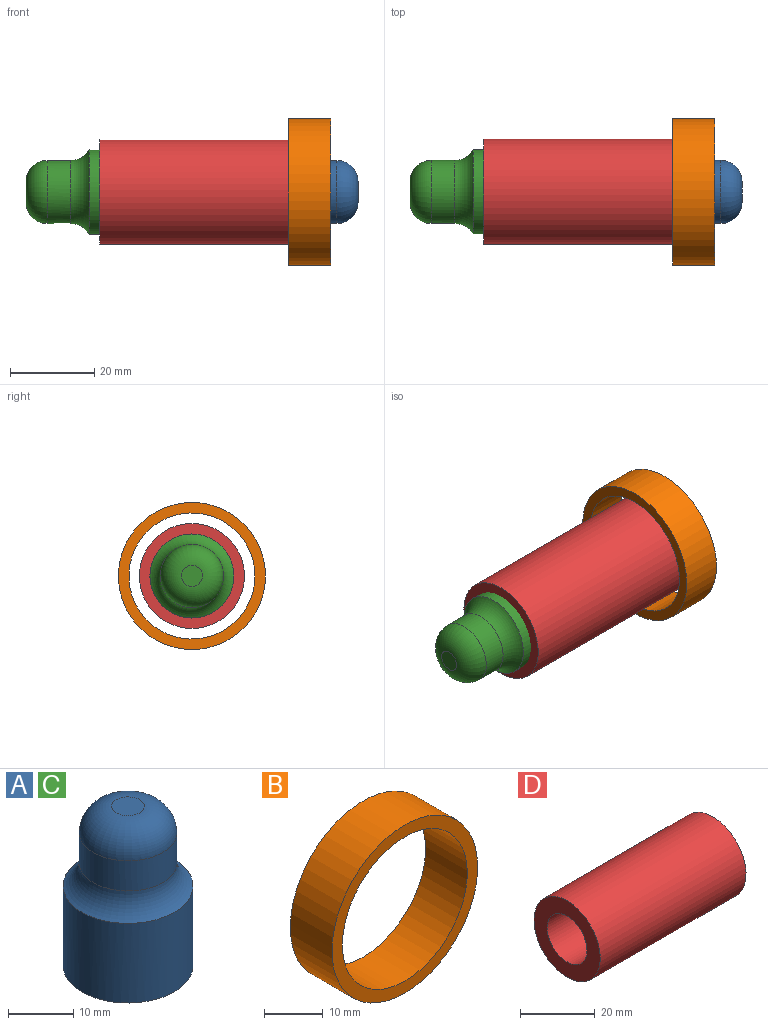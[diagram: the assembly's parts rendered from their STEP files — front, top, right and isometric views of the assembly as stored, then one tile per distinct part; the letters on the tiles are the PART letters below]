
ASSEMBLY  parts=4 mates=3
PART A: 6 faces, bbox 27.1x27.1x30 mm
  f0: cylinder r=10mm len=20mm, axis (0,0,-1), area 942.5mm2, adj f1,f4
  f1: plane 20x20mm, normal (0,0,-1), area 314.2mm2, adj f0
  f2: cylinder r=7.5mm len=15mm, axis (0,0,-1), area 267.2mm2, adj f4,f5
  f3: plane 5x5mm, normal (0,0,1), area 19.6mm2, adj f5
  f4: torus R=12.5mm, axis (0,0,-1), area 275.2mm2, adj f0,f2
  f5: torus R=2.5mm, axis (0,0,1), area 280.4mm2, adj f2,f3
PART B: 4 faces, bbox 35x10x35 mm
  f0: cylinder r=15mm len=30mm, axis (0,-1,0), area 942.5mm2, adj f2,f3
  f1: cylinder r=17.5mm len=35mm, axis (0,-1,0), area 1099.6mm2, adj f2,f3
  f2: plane 35x35mm, normal (0,1,0), area 255.3mm2, adj f0,f1
  f3: plane 35x35mm, normal (0,-1,0), area 255.3mm2, adj f0,f1
PART C: same geometry as A
PART D: 7 faces, bbox 55x25x25 mm
  f0: cylinder r=12.5mm len=55mm, axis (1,0,0), area 4319.7mm2, adj f1,f2
  f1: plane 25x25mm, normal (-1,0,0), area 314.2mm2, adj f0,f5
  f2: plane 25x25mm, normal (1,0,0), area 176.7mm2, adj f0,f3
  f3: cylinder r=10mm len=25mm, axis (1,0,0), area 1570.8mm2, adj f2,f4
  f4: plane 20x20mm, normal (1,0,0), area 314.2mm2, adj f3
  f5: cylinder r=7.5mm len=25mm, axis (-1,0,0), area 1178.1mm2, adj f1,f6
  f6: plane 15x15mm, normal (-1,0,0), area 176.7mm2, adj f5
PLACE A rot(axis=(-0.58,0.58,-0.58),120deg) t=(-8.58,-33.62,24.03)mm
PLACE B rot(axis=(-0.58,0.58,0.58),120deg) t=(14.92,-33.62,24.03)mm
PLACE C rot(axis=(0.71,0,-0.71),180deg) t=(-27.58,-33.62,24.03)mm
PLACE D t=(14.92,-33.62,24.03)mm
MATE cylindrical A.f0 <-> D.f3  axis (-1,0,0) through (-1.08,-33.62,24.03)mm
MATE fastened B.f1 <-> D.f0  axis (1,0,0) through (14.92,-33.62,24.03)mm
MATE fastened C.f0 <-> D.f5  axis (1,0,0) through (-27.58,-33.62,24.03)mm
